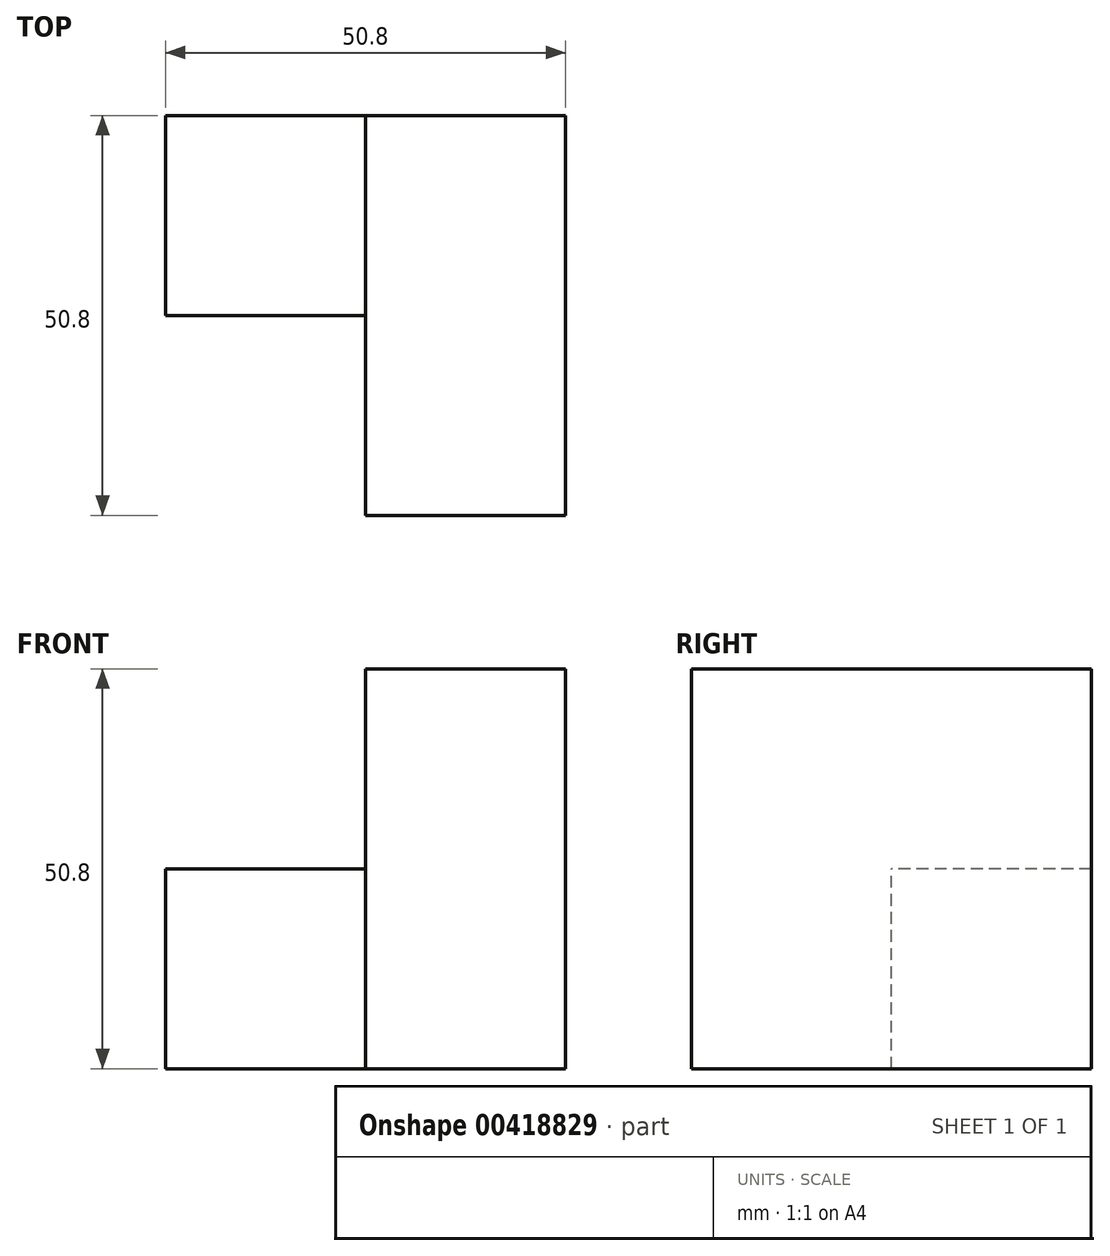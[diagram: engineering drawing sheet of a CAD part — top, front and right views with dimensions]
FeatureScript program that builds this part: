
annotation { "Feature Type Name" : "Feature", "Feature Type Description" : "" }
export const myFeature = defineFeature(function(context is Context, id is Id, definition is map)
    precondition{}
    {
        {
            var Q0;
            Q0=qCreatedBy(makeId("Front.planeOp"),FACE);
            var sketch = newSketch(context, id + "F0", { "sketchPlane" : qUnion([Q0])});
            skLineSegment(sketch, "E0.bottom", {"start": v(0, 0) * mm, "end": v(-25.4, 0) * mm});
            skLineSegment(sketch, "E0.top", {"start": v(0, 50.8) * mm, "end": v(-25.4, 50.8) * mm});
            skLineSegment(sketch, "E0.left", {"start": v(0, 0) * mm, "end": v(0, 50.8) * mm});
            skLineSegment(sketch, "E0.right", {"start": v(-25.4, 0) * mm, "end": v(-25.4, 50.8) * mm});
            skSolve(sketch);
        }
        {
            var Q0;
            Q0 = qSketchRegion(id + "F0", true);
            extrude(context, id + "F1", {"entities" : qUnion([Q0]), "depth" : 50.8 * mm});
        }
        {
            var Q0;
            Q0=makeQuery(id+"F1.opExtrude","SWEPT_FACE",FACE,{"disambiguationData":[OSD([sQuery(id+"F0.wireOp",EDGE,"E0.right")])]});
            var sketch = newSketch(context, id + "F2", { "sketchPlane" : qUnion([Q0])});
            skLineSegment(sketch, "E1.bottom", {"start": v(0, 0) * mm, "end": v(25.4, 0) * mm});
            skLineSegment(sketch, "E1.top", {"start": v(0, 25.4) * mm, "end": v(25.4, 25.4) * mm});
            skLineSegment(sketch, "E1.left", {"start": v(0, 0) * mm, "end": v(0, 25.4) * mm});
            skLineSegment(sketch, "E1.right", {"start": v(25.4, 0) * mm, "end": v(25.4, 25.4) * mm});
            skSolve(sketch);
        }
        {
            var Q0;
            Q0 = qSketchRegion(id + "F2", true);
            extrude(context, id + "F3", {"entities" : qUnion([Q0]), "operationType" : NewBodyOperationType.ADD, "depth" : 25.4 * mm});
        }
    });
